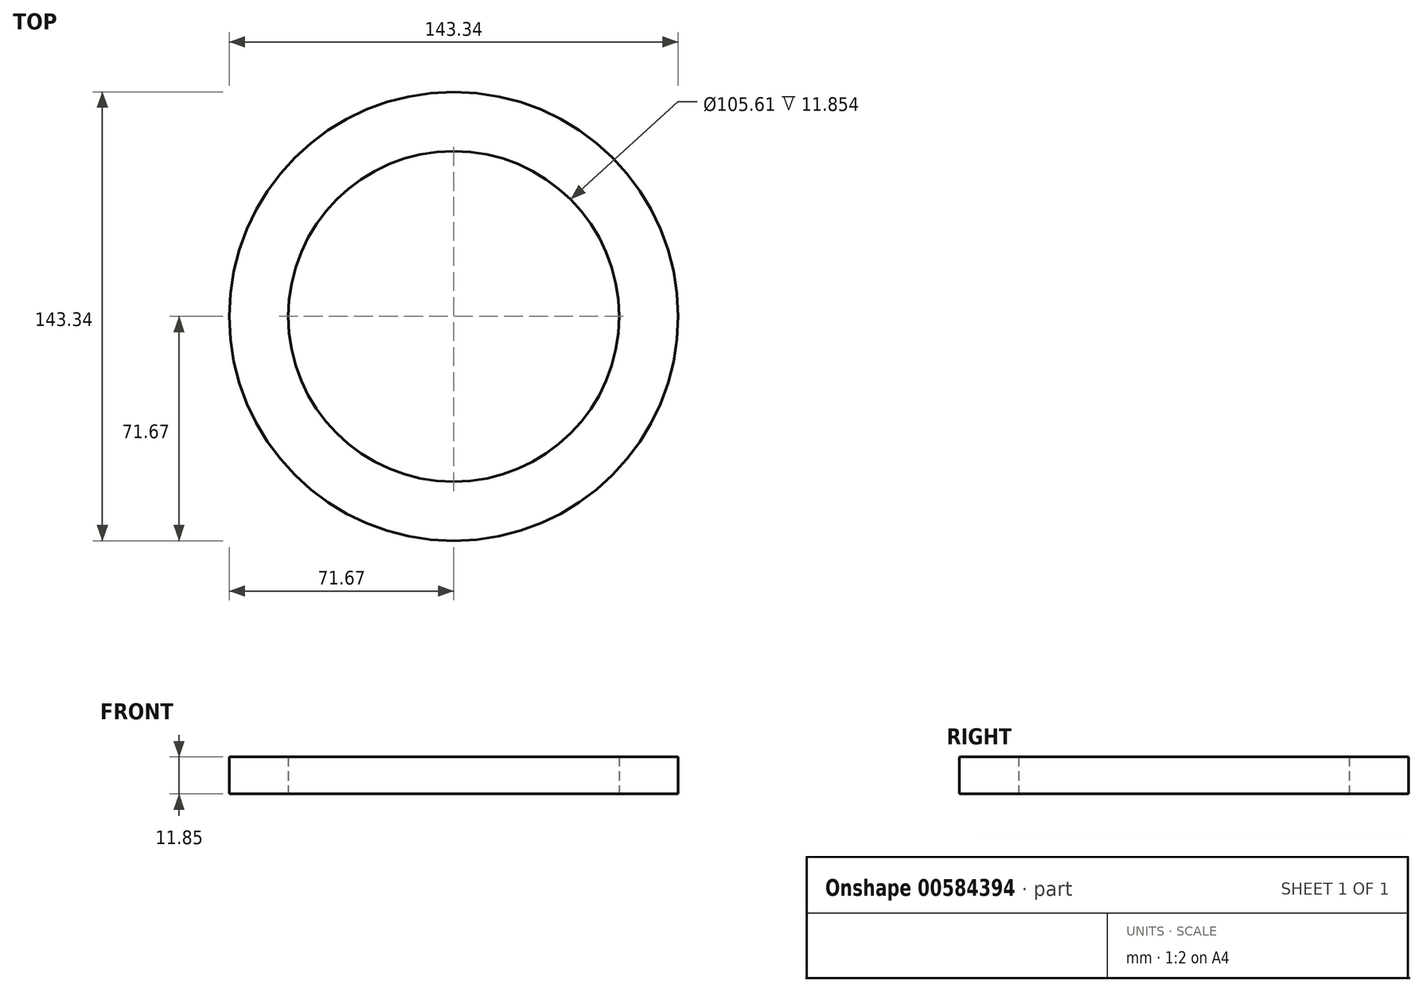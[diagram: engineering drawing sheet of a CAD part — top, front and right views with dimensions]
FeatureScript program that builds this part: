
annotation { "Feature Type Name" : "Feature", "Feature Type Description" : "" }
export const myFeature = defineFeature(function(context is Context, id is Id, definition is map)
    precondition{}
    {
        {
            var Q0;
            Q0=qCreatedBy(makeId("Top.planeOp"),FACE);
            var sketch = newSketch(context, id + "F0", { "sketchPlane" : qUnion([Q0])});
            skCircle(sketch, "E0", {"center": v(0, 0) * mm, "radius": 52.8 * mm});
            skCircle(sketch, "E1", {"center": v(0, 0) * mm, "radius": 71.67 * mm});
            skSolve(sketch);
        }
        {
            var Q0;
            Q0=makeQuery(id+"F0.imprint","IMPRINT",FACE,{"disambiguationData":[TD([[makeQuery(id+"F0.imprint","IMPRINT",EDGE,{"derivedFrom":sQuery(id+"F0.wireOp",EDGE,"E0")}),-1.0]])]});
            extrude(context, id + "F1", {"entities" : qUnion([Q0]), "depth" : 11.85 * mm, "offsetDistance" : 25.4 * mm});
        }
        {
            var Q0;
            Q0=makeQuery(id+"F0.imprint","IMPRINT",FACE,{"disambiguationData":[TD([[makeQuery(id+"F0.imprint","IMPRINT",EDGE,{"derivedFrom":sQuery(id+"F0.wireOp",EDGE,"E0")}),1.0]])]});
            var sketch = newSketch(context, id + "F2", { "sketchPlane" : qUnion([Q0])});
            skCircle(sketch, "E2", {"center": v(0, 0) * mm, "radius": 56.7 * mm});
            skSolve(sketch);
        }
        {
            var Q0;
            Q0 = qSketchRegion(id + "F2", true);
            var Q1;
            Q1=sQuery(id+"F0.wireOp",EDGE,"E0");
            extrude(context, id + "F3", {"entities" : qUnion([Q0]), "bodyType" : ToolBodyType.SURFACE, "surfaceEntities" : qUnion([Q1]), "depth" : 88.26 * mm, "offsetDistance" : 25.4 * mm});
        }
    });
